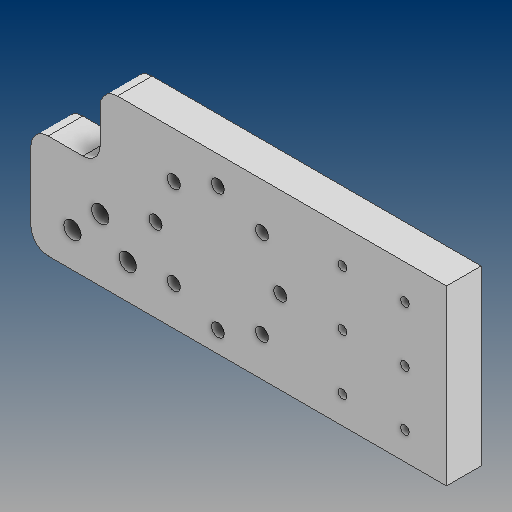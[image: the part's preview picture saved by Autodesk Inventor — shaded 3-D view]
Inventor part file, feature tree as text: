
AUTODESK INVENTOR PART (.ipt)
format: ipt  version: 2020 (Build 240168000, 168)  size: 159,744 bytes
history: native  units: in
note: dims shown in document units (in); Inventor stores cm internally (conversion verified against a paired STEP export)
features: sketch x4, hole x3, extrude x1, other x1, pattern_circular x1, pattern_linear x1, fillet x1
ambient origin geometry x8: Origin, YZ Plane, XZ Plane, XY Plane, X Axis, Y Axis, Z Axis, Center Point
bodies: Solid1 (feature_tree)
feature tree (12):
  extrude  "Extrusion1"  Depth=2.5in
  hole  "Hole1"  [1 undecoded]
  hole  "Hole2"  [1 undecoded]
  other  "Work Axis1"
  pattern_circular  "Circular Pattern1"  [2 undecoded]
  hole  "Hole3"  [1 undecoded]
  pattern_linear  "Rectangular Pattern1"  Spacing1=0.4in  [1 undecoded]
  fillet  "Fillet1"  Radius=1.8in
  sketch  "Sketch1"  dims[d0=6.0in d1=2.5in]
  sketch  "Sketch2"  dims[d2=5.0in d3=1.5in]
  sketch  "Sketch3"  dims[d4=0.5in d5=0.0in d6=5.0in]
  sketch  "Sketch4"  dims[d7=0.4in d8=0.5in d9=0.4in d10=0.4in d11=0.25in d12=0.75in d13=0.375in d14=0.25in d15=0.5635in d16=1.0in d17=0.8108in d18=1.8in d19=3.3in d20=1.2in d25=0.188in d26=0.75in d27=0.375in d28=0.25in d29=0.5635in d30=1.0in d31=0.8108in d32=1.5in d34=3.1496in d35=360.0deg d37=2.0in d38=0.125in d39=0.75in d40=0.375in d41=0.25in d42=0.5635in d43=1.0in d44=0.8108in d45=0.7874in d47=0.9in d48=1.1811in d50=0.8in d51=0.25in]
note: 6 required parameter values undecoded (feature->parameter linkage not recoverable at this tier; creation-order binding heuristic only, values carry confidence <= 0.55)
